# Revit family: Toilet-Floor_Mount-KOHLER-Anglesey-K-4352
name_source: partatom
category: Plumbing Fixtures
revit_build: Autodesk Revit 2017 (Build: 20160225_1515(x64)
units: mm (PartAtom-declared; Revit-internal decimal feet)

## family parameters
Cut with Voids When Loaded = No
Host = Face
OmniClass Number = 23.45.05.21.11
OmniClass Title = Water Closets
Part Type = Normal
Room Calculation Point = No
Round Connector Dimension = Use Diameter
Shared = No

## types (3) — shared parameters
ADA Compliant = Yes
Assembly Code = D2010100
CW Connection = Yes
Cold Water Inlet = Cold Water Inlet
Date Modified = 04/30/2018
Default Elevation = 0"
Environmental Product Declaration = https://www.us.kohler.com
Finish = Kohler-Vitreous_China-0-White
Flow Rate = 0 GPM
Flush Rate = 1.28 or 1.6 GPF
HW Connection = No
Height = 17"
Hot Water Inlet = Hot Water Inlet
Length = 31 1/2"
Manufacturer = KOHLER Co.
MasterFormat 1995 = 15410
MasterFormat 2004 = 22.41.13
Material = Vitreous China
Pressure = 0.00 psi
Product Documentation Link = http://www.us.kohler.com
Product Name = Anglesey
Product Page URL = http://www.us.kohler.com
Rough-In = 4"
Seat Included = No
URL = https://www.us.kohler.com
Vent Connection = No
Waste Connection = Yes
Waste Water Outlet = Waste Water Outlet
WaterSense Certified = Yes
Width = 14 7/8"

## per-type parameters (varying)
| type | 4352_L | Description | Model | Type |
| Elongated bowl, 0-White | No | 1.6 or 1.28 gpf Comfort Height bowl | K-4352-0 | 1 |
| Antimicrobial Finish, Elongated bowl, 0-White | No | 1.6 or 1.28 gpf Comfort Height bowl, antimicrobial | K-4352-SS-0 | 2 |
| Bedpan Lugs, Elongated bowl, 0-White | Yes | 1.6 or 1.28 gpf Comfort Height bowl with bedpan lugs | K-4352-L-0 | 3 |

## geometry (parser evidence)
native form markers: Sweep x4
no freeform markers — native parametric forms only
